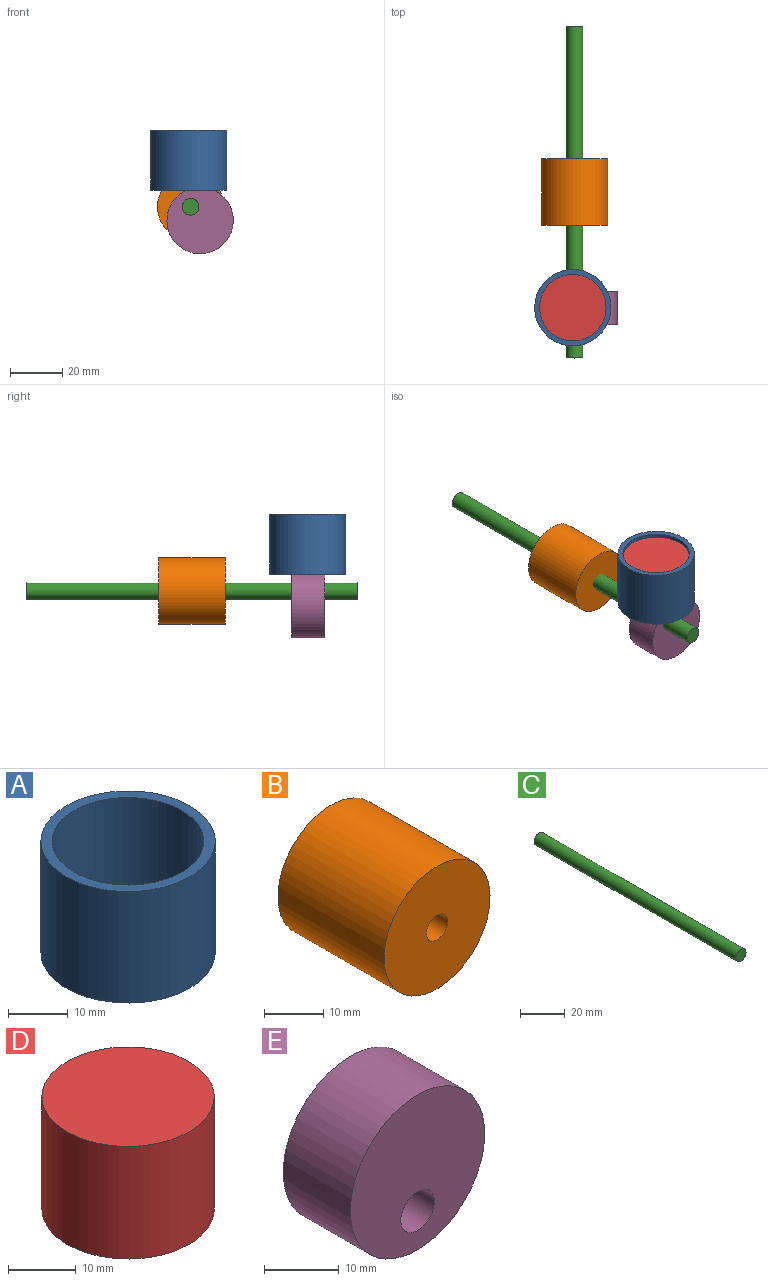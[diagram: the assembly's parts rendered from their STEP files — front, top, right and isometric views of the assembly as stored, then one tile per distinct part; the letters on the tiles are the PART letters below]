
ASSEMBLY  parts=5 mates=3
PART A: 4 faces, bbox 29.2x29.2x22.9 mm
  f0: cylinder r=12.7mm len=25.4mm, axis (0,0,1), area 1824.1mm2, adj f2,f3
  f1: cylinder r=14.61mm len=29.21mm, axis (0,0,1), area 2097.8mm2, adj f2,f3
  f2: plane 29.21x29.21mm, normal (0,0,-1), area 163.4mm2, adj f0,f1
  f3: plane 29.21x29.21mm, normal (0,0,1), area 163.4mm2, adj f0,f1
PART B: 4 faces, bbox 25.4x25.4x25.4 mm
  f0: cylinder r=12.7mm len=25.4mm, axis (0,1,0), area 2026.8mm2, adj f1,f2
  f1: plane 25.4x25.4mm, normal (0,-1,0), area 486.4mm2, adj f0,f3
  f2: plane 25.4x25.4mm, normal (0,1,0), area 486.4mm2, adj f0,f3
  f3: cylinder r=2.54mm len=25.4mm, axis (0,-1,0), area 405.4mm2, adj f1,f2
PART C: 3 faces, bbox 6.4x127x6.4 mm
  f0: cylinder r=3.17mm len=127mm, axis (0,1,0), area 2533.5mm2, adj f1,f2
  f1: plane 6.35x6.35mm, normal (0,-1,0), area 31.7mm2, adj f0
  f2: plane 6.35x6.35mm, normal (0,1,0), area 31.7mm2, adj f0
PART D: 3 faces, bbox 25.4x25.4x20.3 mm
  f0: plane 25.4x25.4mm, normal (0,0,-1), area 506.7mm2, adj f1
  f1: cylinder r=12.7mm len=25.4mm, axis (0,0,1), area 1621.5mm2, adj f0,f2
  f2: plane 25.4x25.4mm, normal (0,0,1), area 506.7mm2, adj f1
PART E: 4 faces, bbox 25.4x12.7x25.4 mm
  f0: cylinder r=12.7mm len=25.4mm, axis (0,1,0), area 1013.4mm2, adj f1,f2
  f1: plane 25.4x25.4mm, normal (0,-1,0), area 475mm2, adj f0,f3
  f2: plane 25.4x25.4mm, normal (0,1,0), area 475mm2, adj f0,f3
  f3: cylinder r=3.17mm len=12.7mm, axis (0,-1,0), area 253.4mm2, adj f1,f2
PLACE A t=(-60.47,6.43,-29.74)mm
PLACE B t=(-59.75,-12.7,-18.02)mm
PLACE C t=(-59.75,0,-18.02)mm fixed
PLACE D t=(-60.47,6.43,-31.19)mm
PLACE E rot(axis=(0,1,0),145.4deg) t=(-59.75,6.35,-18.02)mm
MATE revolute E.f3 <-> C.f0  axis (0,-1,0) through (-59.75,-76.2,-18.02)mm
MATE cylindrical D.f1 <-> A.f0  axis (0,0,-1) through (-60.47,-69.69,-10.55)mm
MATE revolute B.f0 <-> C.f0  axis (0,1,0) through (-59.75,-25.4,-18.02)mm
